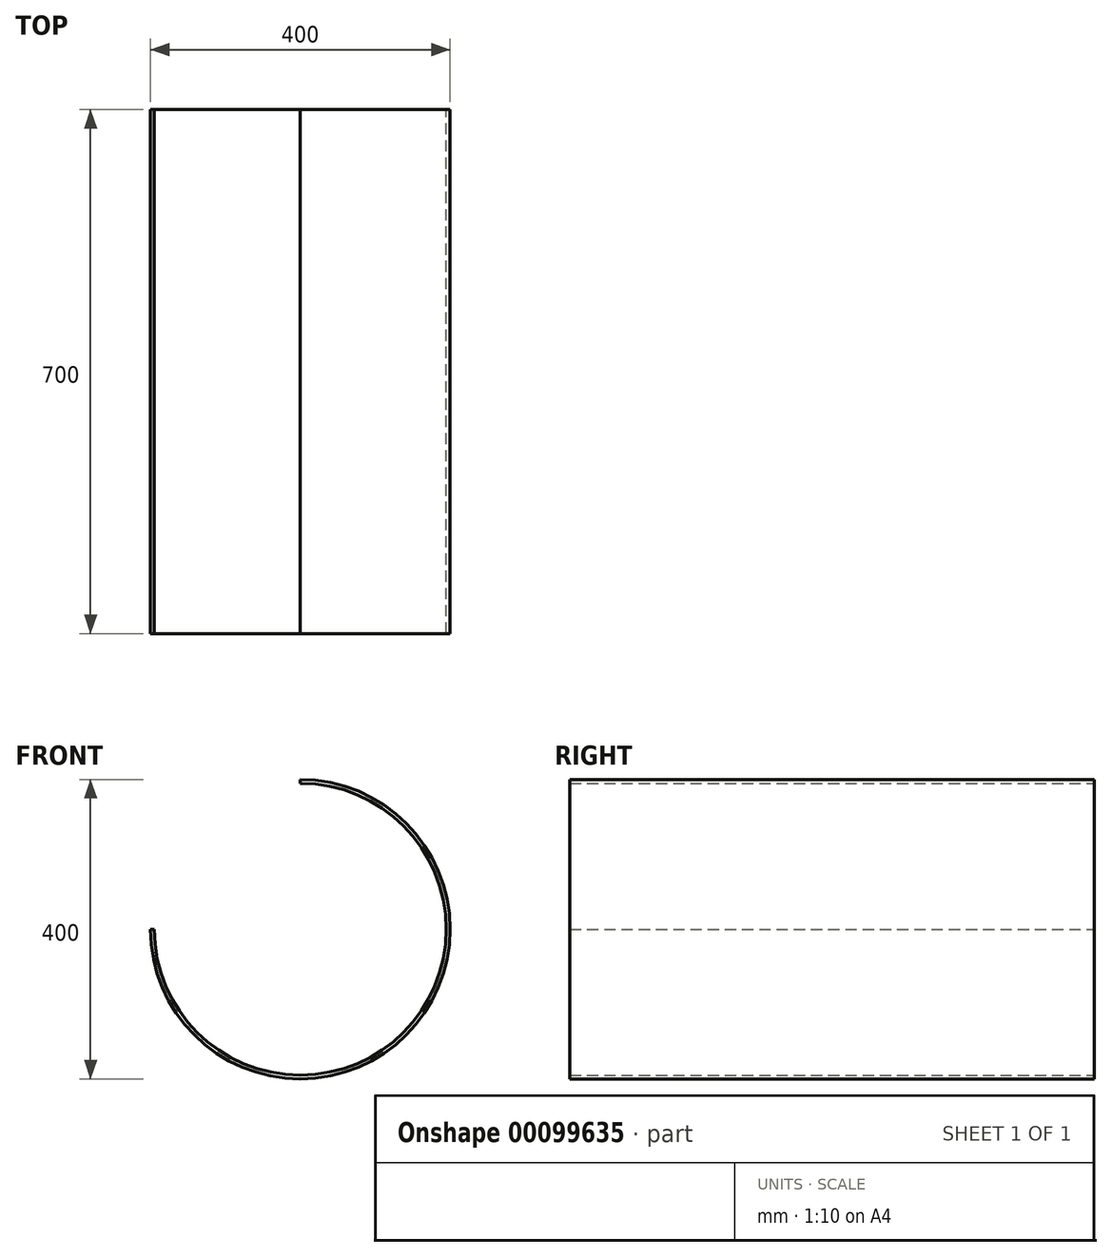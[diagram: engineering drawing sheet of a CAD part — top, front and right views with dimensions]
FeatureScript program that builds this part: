
annotation { "Feature Type Name" : "Feature", "Feature Type Description" : "" }
export const myFeature = defineFeature(function(context is Context, id is Id, definition is map)
    precondition{}
    {
        {
            var Q0;
            Q0=qCreatedBy(makeId("Front.planeOp"),FACE);
            var sketch = newSketch(context, id + "F0", { "sketchPlane" : qUnion([Q0])});
            skArc(sketch, "E0", {"start": v(-200, 0) * mm, "mid": v(141.42, -141.42) * mm, "end": v(0, 200) * mm});
            skArc(sketch, "E1", {"start": v(-195, 0) * mm, "mid": v(137.89, -137.89) * mm, "end": v(0, 195) * mm});
            skLineSegment(sketch, "E2.bottom", {"start": v(-195, 0) * mm, "end": v(-200, 0) * mm});
            skLineSegment(sketch, "E2.left", {"start": v(0, 195) * mm, "end": v(0, 200) * mm});
            skSolve(sketch);
        }
        {
            var Q0;
            Q0=makeQuery(id+"F0.imprint","IMPRINT",FACE,{"disambiguationData":[TD([[makeQuery(id+"F0.imprint","IMPRINT",EDGE,{"derivedFrom":sQuery(id+"F0.wireOp",EDGE,"E0")}),1.0]])]});
            extrude(context, id + "F1", {"entities" : qUnion([Q0]), "endBound" : BoundingType.SYMMETRIC, "depth" : 700 * mm});
        }
        {
            var Q0;
            Q0=makeQuery(id+"F1.opExtrude","CAP_FACE",FACE,{"disambiguationData":[OSD([sQuery(id+"F0.wireOp",EDGE,"E0"),sQuery(id+"F0.wireOp",EDGE,"E1"),sQuery(id+"F0.wireOp",EDGE,"E2.bottom"),sQuery(id+"F0.wireOp",EDGE,"E2.left")])],"isStart":false});
            var sketch = newSketch(context, id + "F2", { "sketchPlane" : qUnion([Q0])});
            skCircle(sketch, "E3", {"center": v(0, 0) * mm, "radius": 200 * mm});
            skCircle(sketch, "E4", {"center": v(0, 0) * mm, "radius": 195 * mm});
            skSolve(sketch);
        }
        {
            var Q0;
            Q0=sQuery(id+"F2.wireOp",EDGE,"E3");
            var Q1;
            Q1=sQuery(id+"F2.wireOp",EDGE,"E4");
            extrude(context, id + "F3", {"bodyType" : ToolBodyType.SURFACE, "surfaceEntities" : qUnion([Q0, Q1]), "depth" : 150 * mm});
        }
        {
            var Q0;
            Q0=makeQuery(id+"F3.opExtrude","SWEPT_BODY",BODY,{"disambiguationData":[OSD([sQuery(id+"F2.wireOp",EDGE,"E3")])]});
            var Q1;
            Q1=qCreatedBy(makeId("Front.planeOp"),FACE);
            mirror(context, id + "F4", {"entities" : qUnion([Q0]), "mirrorPlane" : qUnion([Q1])});
        }
        {
            var Q0;
            Q0=makeQuery(id+"F3.opExtrude","SWEPT_BODY",BODY,{"disambiguationData":[OSD([sQuery(id+"F2.wireOp",EDGE,"E4")])]});
            var Q1;
            Q1=qCreatedBy(makeId("Front.planeOp"),FACE);
            mirror(context, id + "F5", {"entities" : qUnion([Q0]), "mirrorPlane" : qUnion([Q1])});
        }
    });
